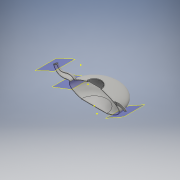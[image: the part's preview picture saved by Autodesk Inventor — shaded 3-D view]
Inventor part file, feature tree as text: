
AUTODESK INVENTOR PART (.ipt)
format: ipt  version: 2016 (Build 200138000, 138)  size: 559,104 bytes
history: native  units: in
note: dims shown in document units (in); Inventor stores cm internally (conversion verified against a paired STEP export)
features: sketch x10, delete_face x4, plane x3, other x2, surface_op x2, revolve x1, loft x1, shell x1, sweep x1
ambient origin geometry x8: Origin, YZ Plane, XZ Plane, XY Plane, X Axis, Y Axis, Z Axis, Center Point
bodies: Solid1 (feature_tree)
feature tree (25):
  other  "CrossSection1"
  revolve  "Revolution1"  [1 undecoded]
  sketch  "Sketch2"  dims[d3=0.0in d4=90.0deg d5=0.0in d6=90.0deg d7=0.0in d8=90.0deg]
  plane  "Work Plane1"
  sketch  "Sketch4"  dims[d14=0.1969in]
  sketch  "Sketch5"  dims[d15=0.0in]
  sketch  "Sketch6"
  plane  "Work Plane2"
  plane  "Work Plane3"
  loft  "Loft1"
  sketch  "Sketch9"
  shell  "Shell1"  Thickness=0.0in
  sweep  "Sweep1"
  delete_face  "Delete Face1"
  delete_face  "Delete Face2"
  surface_op  "Stitch Surface1"
  sketch  "Sketch10"
  delete_face  "Delete Face3"
  delete_face  "Delete Face4"
  sketch  "Sketch1"  dims[d0=90.0deg d1=0.0in d2=0.0in]
  sketch  "Sketch3"  dims[d9=0.02in d10=0.013in d11=0.5in d12=0.0in d13=2.0in]
  sketch  "Sketch7"
  sketch  "Sketch8"
  other  "Srf1"
  surface_op  "Boundary Patch1"
note: 1 required parameter value undecoded (feature->parameter linkage not recoverable at this tier; creation-order binding heuristic only, values carry confidence <= 0.55)
